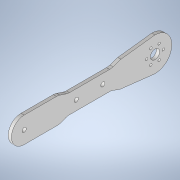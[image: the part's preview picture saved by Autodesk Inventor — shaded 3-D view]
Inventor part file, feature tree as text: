
AUTODESK INVENTOR PART (.ipt)
format: ipt  version: 2022 (Build 260153000, 153)  size: 178,176 bytes
history: native  units: mm
features: fillet x6, extrude x1, sketch x1
ambient origin geometry x8: Origin, YZ Plane, XZ Plane, XY Plane, X Axis, Y Axis, Z Axis, Center Point
bodies: Body1 (feature_tree)
feature tree (8):
  extrude  "Extrusion2"  Depth=18.0mm
  fillet  "Face Fillet1"
  fillet  "Face Fillet2"
  fillet  "Face Fillet3"
  fillet  "Face Fillet5"
  fillet  "Face Fillet6"
  fillet  "Face Fillet7"
  sketch  "Sketch1"  dims[d6=8.75mm d7=18.0mm d8=1.2mm d12=4.0mm d13=60.0mm d15=360.0deg d18=24.0mm d22=45.0mm d23=8.0mm d24=9.0mm d25=9.0mm d33=8.0mm d34=12.5mm d35=3.0mm d36=0.0mm d37=10.0mm d38=10.0mm d39=10.0mm d41=10.0mm d42=10.0mm d43=10.0mm d45=4.0mm]
